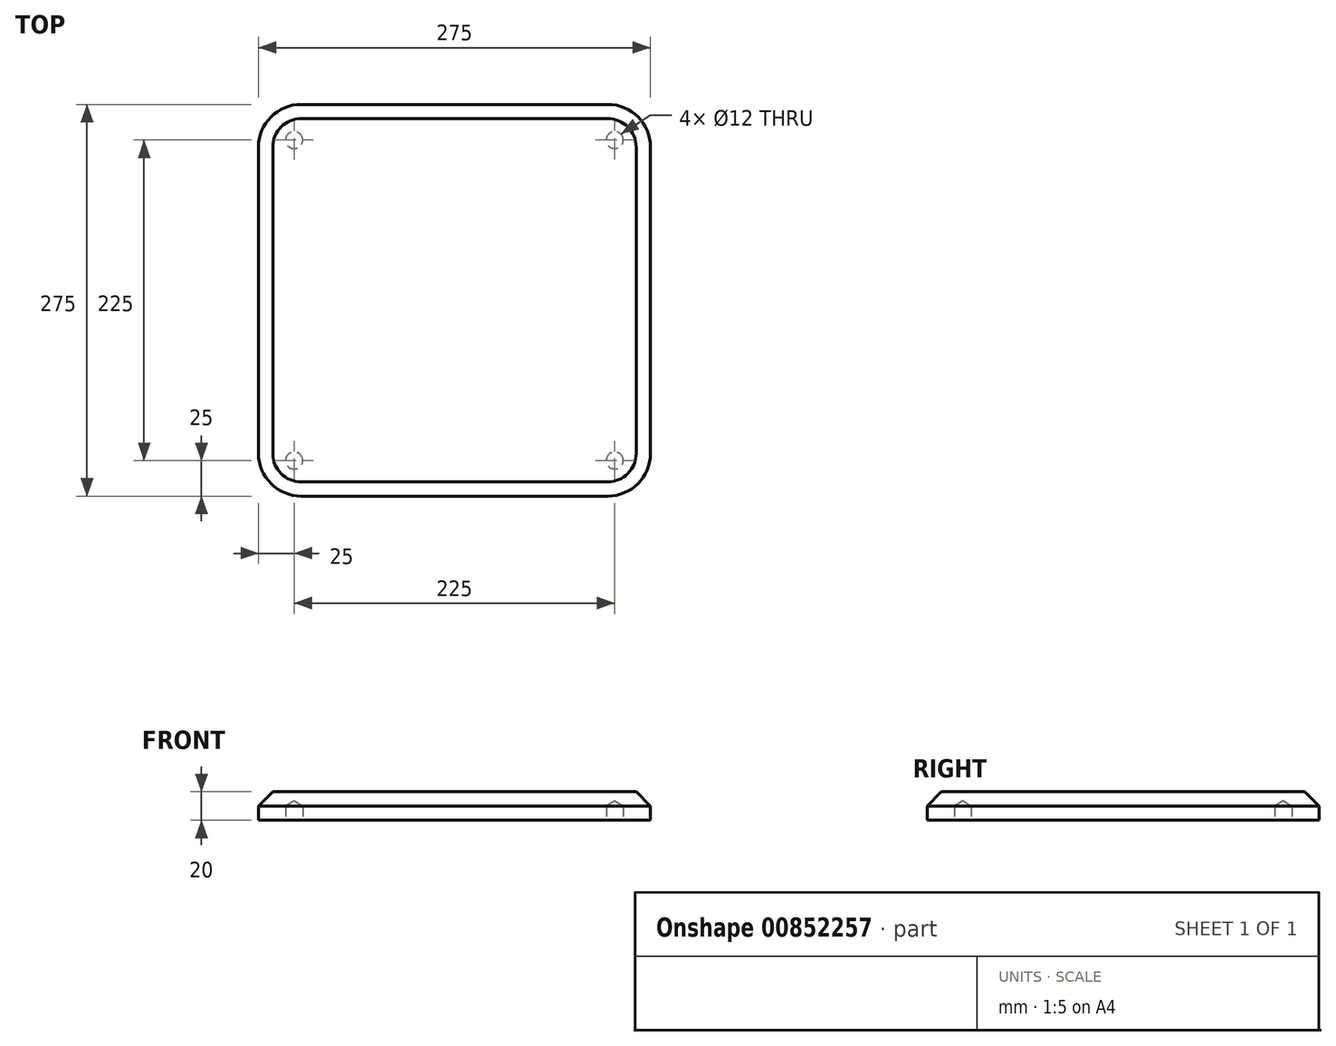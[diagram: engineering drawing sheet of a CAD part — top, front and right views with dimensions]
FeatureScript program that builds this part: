
annotation { "Feature Type Name" : "Feature", "Feature Type Description" : "" }
export const myFeature = defineFeature(function(context is Context, id is Id, definition is map)
    precondition{}
    {
        {
            var Q0;
            Q0=qCreatedBy(makeId("Top.planeOp"),FACE);
            var sketch = newSketch(context, id + "F0", { "sketchPlane" : qUnion([Q0])});
            skLineSegment(sketch, "E0.bottom", {"start": v(-107.5, 137.5) * mm, "end": v(107.5, 137.5) * mm});
            skLineSegment(sketch, "E0.top", {"start": v(-107.5, -137.5) * mm, "end": v(107.5, -137.5) * mm});
            skLineSegment(sketch, "E0.left", {"start": v(-137.5, 107.5) * mm, "end": v(-137.5, -107.5) * mm});
            skLineSegment(sketch, "E0.right", {"start": v(137.5, 107.5) * mm, "end": v(137.5, -107.5) * mm});
            skPoint(sketch, "E0.middle", {"position": v(0, 0) * mm});
            skPoint(sketch, "E1.visualSharp", {"position": v(-137.5, 137.5) * mm});
            skArc(sketch, "E1.filletArc", {"start": v(-107.5, 137.5) * mm, "mid": v(-128.71, 128.71) * mm, "end": v(-137.5, 107.5) * mm});
            skPoint(sketch, "E2.visualSharp", {"position": v(137.5, 137.5) * mm});
            skArc(sketch, "E2.filletArc", {"start": v(137.5, 107.5) * mm, "mid": v(128.71, 128.71) * mm, "end": v(107.5, 137.5) * mm});
            skPoint(sketch, "E3.visualSharp", {"position": v(137.5, -137.5) * mm});
            skArc(sketch, "E3.filletArc", {"start": v(107.5, -137.5) * mm, "mid": v(128.71, -128.71) * mm, "end": v(137.5, -107.5) * mm});
            skPoint(sketch, "E4.visualSharp", {"position": v(-137.5, -137.5) * mm});
            skArc(sketch, "E4.filletArc", {"start": v(-137.5, -107.5) * mm, "mid": v(-128.71, -128.71) * mm, "end": v(-107.5, -137.5) * mm});
            skSolve(sketch);
        }
        {
            var Q0;
            Q0 = qSketchRegion(id + "F0", true);
            extrude(context, id + "F1", {"entities" : qUnion([Q0]), "depth" : 20 * mm, "offsetDistance" : 25 * mm});
        }
        {
            var Q0;
            Q0=makeQuery(id+"F1.opExtrude","CAP_EDGE",EDGE,{"disambiguationData":[OSD([sQuery(id+"F0.wireOp",EDGE,"E0.left")])],"isStart":false});
            chamfer(context, id + "F2", {"entities" : qUnion([Q0]), "width" : 10 * mm, "tangentPropagation" : true});
        }
        {
            var Q0;
            Q0=makeQuery(id+"F1.opExtrude","CAP_FACE",FACE,{"disambiguationData":[OSD([sQuery(id+"F0.wireOp",EDGE,"E0.bottom"),sQuery(id+"F0.wireOp",EDGE,"E0.top"),sQuery(id+"F0.wireOp",EDGE,"E0.left"),sQuery(id+"F0.wireOp",EDGE,"E0.right"),sQuery(id+"F0.wireOp",EDGE,"E1.filletArc"),sQuery(id+"F0.wireOp",EDGE,"E2.filletArc"),sQuery(id+"F0.wireOp",EDGE,"E3.filletArc"),sQuery(id+"F0.wireOp",EDGE,"E4.filletArc")])],"isStart":true});
            var sketch = newSketch(context, id + "F3", { "sketchPlane" : qUnion([Q0])});
            skPoint(sketch, "E5.middle", {"position": v(0, 0) * mm});
            skLineSegment(sketch, "E6.bottom", {"start": v(-112.5, 112.5) * mm, "end": v(112.5, 112.5) * mm, "construction": true});
            skLineSegment(sketch, "E6.top", {"start": v(-112.5, -112.5) * mm, "end": v(112.5, -112.5) * mm, "construction": true});
            skLineSegment(sketch, "E6.left", {"start": v(-112.5, 112.5) * mm, "end": v(-112.5, -112.5) * mm, "construction": true});
            skLineSegment(sketch, "E6.right", {"start": v(112.5, 112.5) * mm, "end": v(112.5, -112.5) * mm, "construction": true});
            skSolve(sketch);
        }
        {
            var Q0;
            Q0=sQuery(id+"F3.wireOp",VERTEX,"E6.bottom.start");
            var Q1;
            Q1=sQuery(id+"F3.wireOp",VERTEX,"E6.bottom.end");
            var Q2;
            Q2=sQuery(id+"F3.wireOp",VERTEX,"E6.top.end");
            var Q3;
            Q3=sQuery(id+"F3.wireOp",VERTEX,"E6.top.start");
            var Q4;
            Q4=makeQuery(id+"F1.opExtrude","SWEPT_BODY",BODY,{"disambiguationData":[OSD([sQuery(id+"F0.wireOp",EDGE,"E0.bottom"),sQuery(id+"F0.wireOp",EDGE,"E0.top"),sQuery(id+"F0.wireOp",EDGE,"E0.left"),sQuery(id+"F0.wireOp",EDGE,"E0.right"),sQuery(id+"F0.wireOp",EDGE,"E1.filletArc"),sQuery(id+"F0.wireOp",EDGE,"E2.filletArc"),sQuery(id+"F0.wireOp",EDGE,"E3.filletArc"),sQuery(id+"F0.wireOp",EDGE,"E4.filletArc")])]});
            hole(context, id + "F4", {"style" : HoleStyle.SIMPLE, "endStyle" : HoleEndStyle.BLIND, "holeDiameter" : 12 * mm, "majorDiameter" : 5 * mm, "holeDepth" : 10 * mm, "isTappedThrough" : true, "tappedDepth" : 12 * mm, "tapClearance" : 3, "locations" : qUnion([Q0, Q1, Q2, Q3]), "scope" : qUnion([Q4])});
        }
    });
